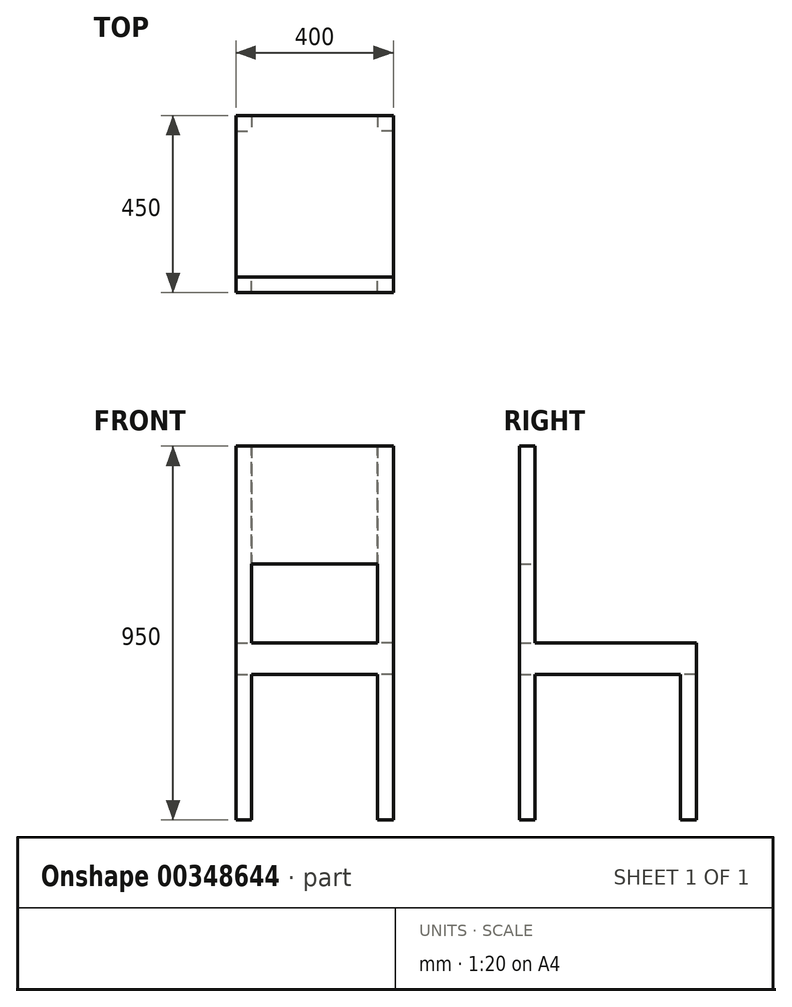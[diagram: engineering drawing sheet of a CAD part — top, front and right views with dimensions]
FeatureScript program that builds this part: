
annotation { "Feature Type Name" : "Feature", "Feature Type Description" : "" }
export const myFeature = defineFeature(function(context is Context, id is Id, definition is map)
    precondition{}
    {
        {
            var Q0;
            Q0=qCreatedBy(makeId("Top.planeOp"),FACE);
            var sketch = newSketch(context, id + "F0", { "sketchPlane" : qUnion([Q0])});
            skLineSegment(sketch, "E0.bottom", {"start": v(0, 0) * mm, "end": v(400, 0) * mm});
            skLineSegment(sketch, "E0.top", {"start": v(0, 450) * mm, "end": v(400, 450) * mm});
            skLineSegment(sketch, "E0.left", {"start": v(0, 0) * mm, "end": v(0, 450) * mm});
            skLineSegment(sketch, "E0.right", {"start": v(400, 0) * mm, "end": v(400, 450) * mm});
            skSolve(sketch);
        }
        {
            var Q0;
            Q0=makeQuery(id+"F0.imprint","IMPRINT",FACE,{"disambiguationData":[TD([[makeQuery(id+"F0.imprint","IMPRINT",EDGE,{"derivedFrom":sQuery(id+"F0.wireOp",EDGE,"E0.bottom")}),1.0]])]});
            extrude(context, id + "F1", {"entities" : qUnion([Q0]), "oppositeDirection" : true, "depth" : 80 * mm});
        }
        {
            var Q0;
            Q0=makeQuery(id+"F1.opExtrude","CAP_FACE",FACE,{"disambiguationData":[OSD([sQuery(id+"F0.wireOp",EDGE,"E0.bottom"),sQuery(id+"F0.wireOp",EDGE,"E0.top"),sQuery(id+"F0.wireOp",EDGE,"E0.left"),sQuery(id+"F0.wireOp",EDGE,"E0.right")])],"isStart":true});
            var sketch = newSketch(context, id + "F2", { "sketchPlane" : qUnion([Q0])});
            skLineSegment(sketch, "E1.bottom", {"start": v(0, 450) * mm, "end": v(40, 450) * mm});
            skLineSegment(sketch, "E1.top", {"start": v(0, 410) * mm, "end": v(40, 410) * mm});
            skLineSegment(sketch, "E1.left", {"start": v(0, 450) * mm, "end": v(0, 410) * mm});
            skLineSegment(sketch, "E1.right", {"start": v(40, 450) * mm, "end": v(40, 410) * mm});
            skLineSegment(sketch, "E2.bottom", {"start": v(400, 450) * mm, "end": v(360, 450) * mm});
            skLineSegment(sketch, "E2.top", {"start": v(400, 410) * mm, "end": v(360, 410) * mm});
            skLineSegment(sketch, "E2.left", {"start": v(400, 450) * mm, "end": v(400, 410) * mm});
            skLineSegment(sketch, "E2.right", {"start": v(360, 450) * mm, "end": v(360, 410) * mm});
            skLineSegment(sketch, "E3.bottom", {"start": v(0, 0) * mm, "end": v(40, 0) * mm});
            skLineSegment(sketch, "E3.top", {"start": v(0, 40) * mm, "end": v(40, 40) * mm});
            skLineSegment(sketch, "E3.left", {"start": v(0, 0) * mm, "end": v(0, 40) * mm});
            skLineSegment(sketch, "E3.right", {"start": v(40, 0) * mm, "end": v(40, 40) * mm});
            skLineSegment(sketch, "E4.bottom", {"start": v(400, 0) * mm, "end": v(360, 0) * mm});
            skLineSegment(sketch, "E4.top", {"start": v(400, 40) * mm, "end": v(360, 40) * mm});
            skLineSegment(sketch, "E4.left", {"start": v(400, 0) * mm, "end": v(400, 40) * mm});
            skLineSegment(sketch, "E4.right", {"start": v(360, 0) * mm, "end": v(360, 40) * mm});
            skSolve(sketch);
        }
        {
            var Q0;
            Q0=makeQuery(id+"F2.imprint","IMPRINT",FACE,{"disambiguationData":[TD([[makeQuery(id+"F2.imprint","IMPRINT",EDGE,{"derivedFrom":sQuery(id+"F2.wireOp",EDGE,"E3.bottom")}),1.0]])]});
            var Q1;
            Q1=makeQuery(id+"F2.imprint","IMPRINT",FACE,{"disambiguationData":[TD([[makeQuery(id+"F2.imprint","IMPRINT",EDGE,{"derivedFrom":sQuery(id+"F2.wireOp",EDGE,"E4.bottom")}),1.0]])]});
            extrude(context, id + "F3", {"entities" : qUnion([Q0, Q1]), "operationType" : NewBodyOperationType.ADD, "depth" : 500 * mm});
        }
        {
            var Q0;
            Q0=makeQuery(id+"F2.imprint","IMPRINT",FACE,{"disambiguationData":[TD([[makeQuery(id+"F2.imprint","IMPRINT",EDGE,{"derivedFrom":sQuery(id+"F2.wireOp",EDGE,"E3.bottom")}),1.0]])]});
            var Q1;
            Q1=makeQuery(id+"F2.imprint","IMPRINT",FACE,{"disambiguationData":[TD([[makeQuery(id+"F2.imprint","IMPRINT",EDGE,{"derivedFrom":sQuery(id+"F2.wireOp",EDGE,"E4.bottom")}),1.0]])]});
            var Q2;
            Q2=makeQuery(id+"F2.imprint","IMPRINT",FACE,{"disambiguationData":[TD([[makeQuery(id+"F2.imprint","IMPRINT",EDGE,{"derivedFrom":sQuery(id+"F2.wireOp",EDGE,"E2.bottom")}),-1.0]])]});
            var Q3;
            Q3=makeQuery(id+"F2.imprint","IMPRINT",FACE,{"disambiguationData":[TD([[makeQuery(id+"F2.imprint","IMPRINT",EDGE,{"derivedFrom":sQuery(id+"F2.wireOp",EDGE,"E1.bottom")}),-1.0]])]});
            extrude(context, id + "F4", {"entities" : qUnion([Q0, Q1, Q2, Q3]), "operationType" : NewBodyOperationType.ADD, "oppositeDirection" : true, "depth" : 450 * mm});
        }
        {
            var Q0;
            Q0=makeQuery(id+"F3.opExtrude","CAP_FACE",FACE,{"disambiguationData":[OSD([sQuery(id+"F2.wireOp",EDGE,"E3.bottom"),sQuery(id+"F2.wireOp",EDGE,"E3.top"),sQuery(id+"F2.wireOp",EDGE,"E3.left"),sQuery(id+"F2.wireOp",EDGE,"E3.right")])],"isStart":false});
            var sketch = newSketch(context, id + "F5", { "sketchPlane" : qUnion([Q0])});
            skLineSegment(sketch, "E5.bottom", {"start": v(0, 0) * mm, "end": v(400, 0) * mm});
            skLineSegment(sketch, "E5.top", {"start": v(0, 39.55) * mm, "end": v(400, 39.55) * mm});
            skLineSegment(sketch, "E5.left", {"start": v(0, 0) * mm, "end": v(0, 39.55) * mm});
            skLineSegment(sketch, "E5.right", {"start": v(400, 0) * mm, "end": v(400, 39.55) * mm});
            skSolve(sketch);
        }
        {
            var Q0;
            {var subQ3=sQuery(id+"F5.wireOp",EDGE,"E5.right");Q0=makeQuery(id+"F5.imprint","IMPRINT",FACE,{"disambiguationData":[TD([[makeQuery(id+"F5.imprint","IMPRINT",EDGE,{"derivedFrom":subQ3}),1.0]])]});}
            extrude(context, id + "F6", {"entities" : qUnion([Q0]), "operationType" : NewBodyOperationType.ADD, "oppositeDirection" : true, "depth" : 300 * mm});
        }
    });
